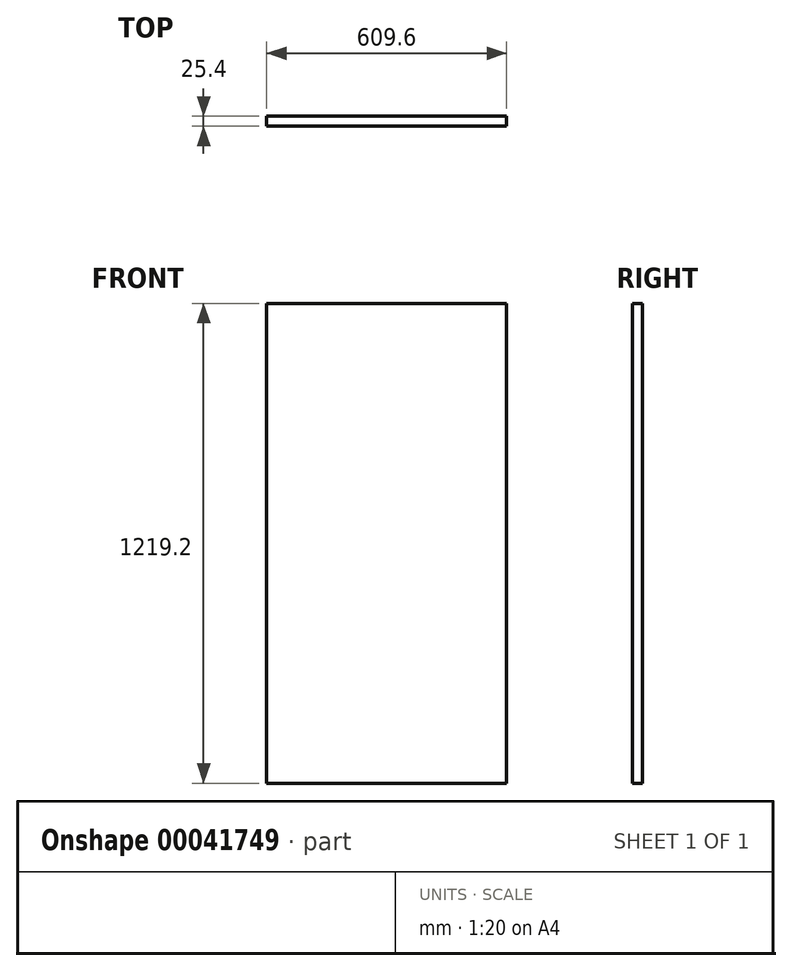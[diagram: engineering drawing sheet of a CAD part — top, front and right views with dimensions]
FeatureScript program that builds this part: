
annotation { "Feature Type Name" : "Feature", "Feature Type Description" : "" }
export const myFeature = defineFeature(function(context is Context, id is Id, definition is map)
    precondition{}
    {
        {
            var Q0;
            Q0=qCreatedBy(makeId("Front.planeOp"),FACE);
            var sketch = newSketch(context, id + "F0", { "sketchPlane" : qUnion([Q0])});
            skLineSegment(sketch, "E0.bottom", {"start": v(-304.8, 609.6) * mm, "end": v(304.8, 609.6) * mm});
            skLineSegment(sketch, "E0.top", {"start": v(-304.8, -609.6) * mm, "end": v(304.8, -609.6) * mm});
            skLineSegment(sketch, "E0.left", {"start": v(-304.8, 609.6) * mm, "end": v(-304.8, -609.6) * mm});
            skLineSegment(sketch, "E0.right", {"start": v(304.8, 609.6) * mm, "end": v(304.8, -609.6) * mm});
            skPoint(sketch, "E0.middle", {"position": v(0, 0) * mm});
            skSolve(sketch);
        }
        {
            var Q0;
            Q0 = qSketchRegion(id + "F0", true);
            extrude(context, id + "F1", {"entities" : qUnion([Q0]), "depth" : 25.4 * mm});
        }
    });
